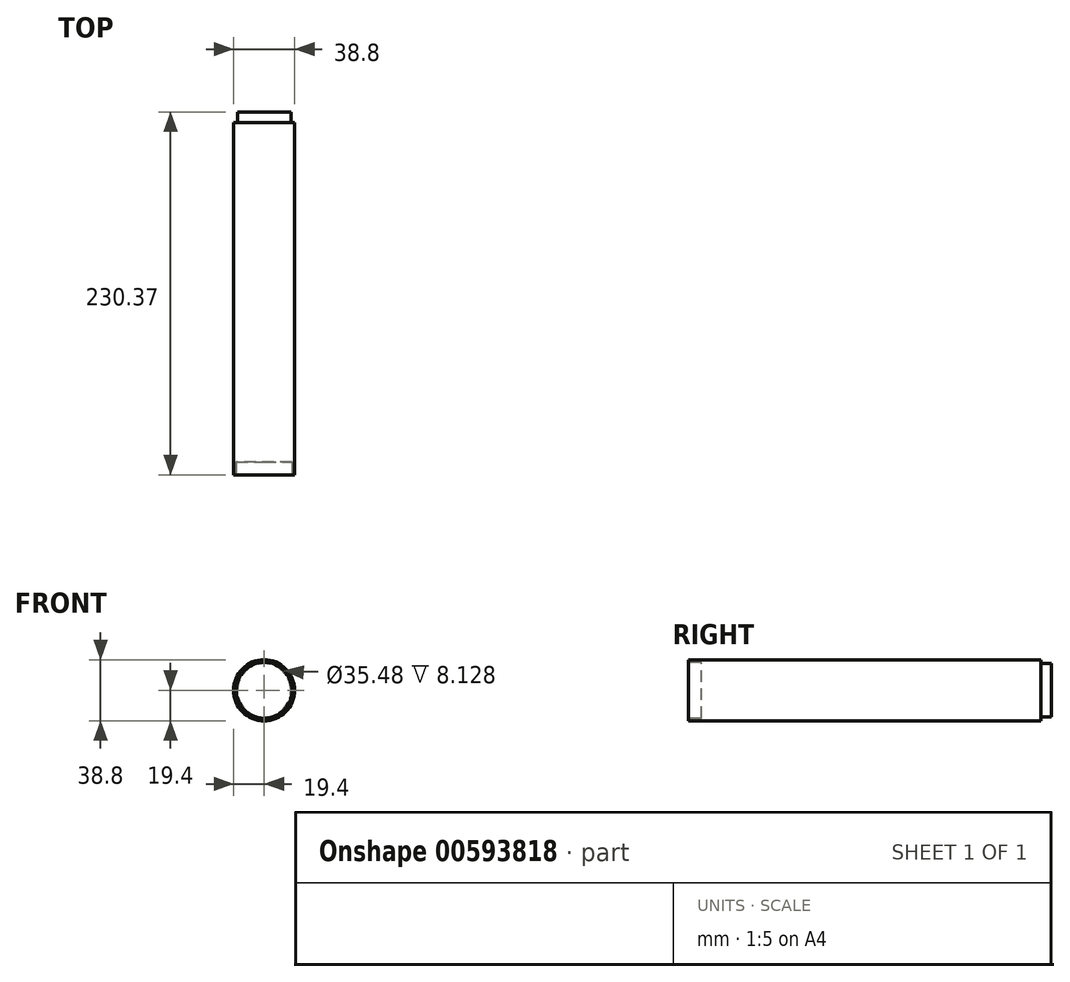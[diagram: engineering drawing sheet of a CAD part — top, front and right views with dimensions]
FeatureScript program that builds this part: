
annotation { "Feature Type Name" : "Feature", "Feature Type Description" : "" }
export const myFeature = defineFeature(function(context is Context, id is Id, definition is map)
    precondition{}
    {
        {
            var Q0;
            Q0=qCreatedBy(makeId("Front.planeOp"),FACE);
            var sketch = newSketch(context, id + "F0", { "sketchPlane" : qUnion([Q0])});
            skCircle(sketch, "E0", {"center": v(0, 0) * mm, "radius": 19.4 * mm});
            skSolve(sketch);
        }
        {
            var Q0;
            Q0=makeQuery(id+"F0.imprint","IMPRINT",FACE,{"disambiguationData":[TD([[makeQuery(id+"F0.imprint","IMPRINT",EDGE,{"derivedFrom":sQuery(id+"F0.wireOp",EDGE,"E0")}),1.0]])]});
            extrude(context, id + "F1", {"entities" : qUnion([Q0]), "depth" : 223.77 * mm, "offsetDistance" : 25.4 * mm});
        }
        {
            var Q0;
            Q0=makeQuery(id+"F1.opExtrude","CAP_FACE",FACE,{"disambiguationData":[OSD([sQuery(id+"F0.wireOp",EDGE,"E0")])],"isStart":true});
            var sketch = newSketch(context, id + "F2", { "sketchPlane" : qUnion([Q0])});
            skCircle(sketch, "E1", {"center": v(0, 0) * mm, "radius": 16.96 * mm});
            skSolve(sketch);
        }
        {
            var Q0;
            Q0 = qSketchRegion(id + "F2", true);
            extrude(context, id + "F3", {"entities" : qUnion([Q0]), "operationType" : NewBodyOperationType.ADD, "depth" : 6.6 * mm, "offsetDistance" : 25.4 * mm});
        }
        {
            var Q0;
            Q0=makeQuery(id+"F1.opExtrude","CAP_FACE",FACE,{"disambiguationData":[OSD([sQuery(id+"F0.wireOp",EDGE,"E0")])],"isStart":false});
            extrude(context, id + "F4", {"entities" : qUnion([Q0]), "operationType" : NewBodyOperationType.ADD, "oppositeDirection" : true, "depth" : 5.08 * mm, "offsetDistance" : 25.4 * mm});
        }
        {
            var Q0;
            Q0=makeQuery(id+"F1.opExtrude","CAP_FACE",FACE,{"disambiguationData":[OSD([sQuery(id+"F0.wireOp",EDGE,"E0")])],"isStart":false});
            var sketch = newSketch(context, id + "F5", { "sketchPlane" : qUnion([Q0])});
            skCircle(sketch, "E2", {"center": v(0, 0) * mm, "radius": 17.74 * mm});
            skSolve(sketch);
        }
        {
            var Q0;
            Q0=makeQuery(id+"F5.imprint","IMPRINT",FACE,{"disambiguationData":[TD([[makeQuery(id+"F5.imprint","IMPRINT",EDGE,{"derivedFrom":sQuery(id+"F5.wireOp",EDGE,"E2")}),1.0]])]});
            extrude(context, id + "F6", {"entities" : qUnion([Q0]), "operationType" : NewBodyOperationType.REMOVE, "oppositeDirection" : true, "depth" : 8.13 * mm, "offsetDistance" : 25.4 * mm});
        }
    });
